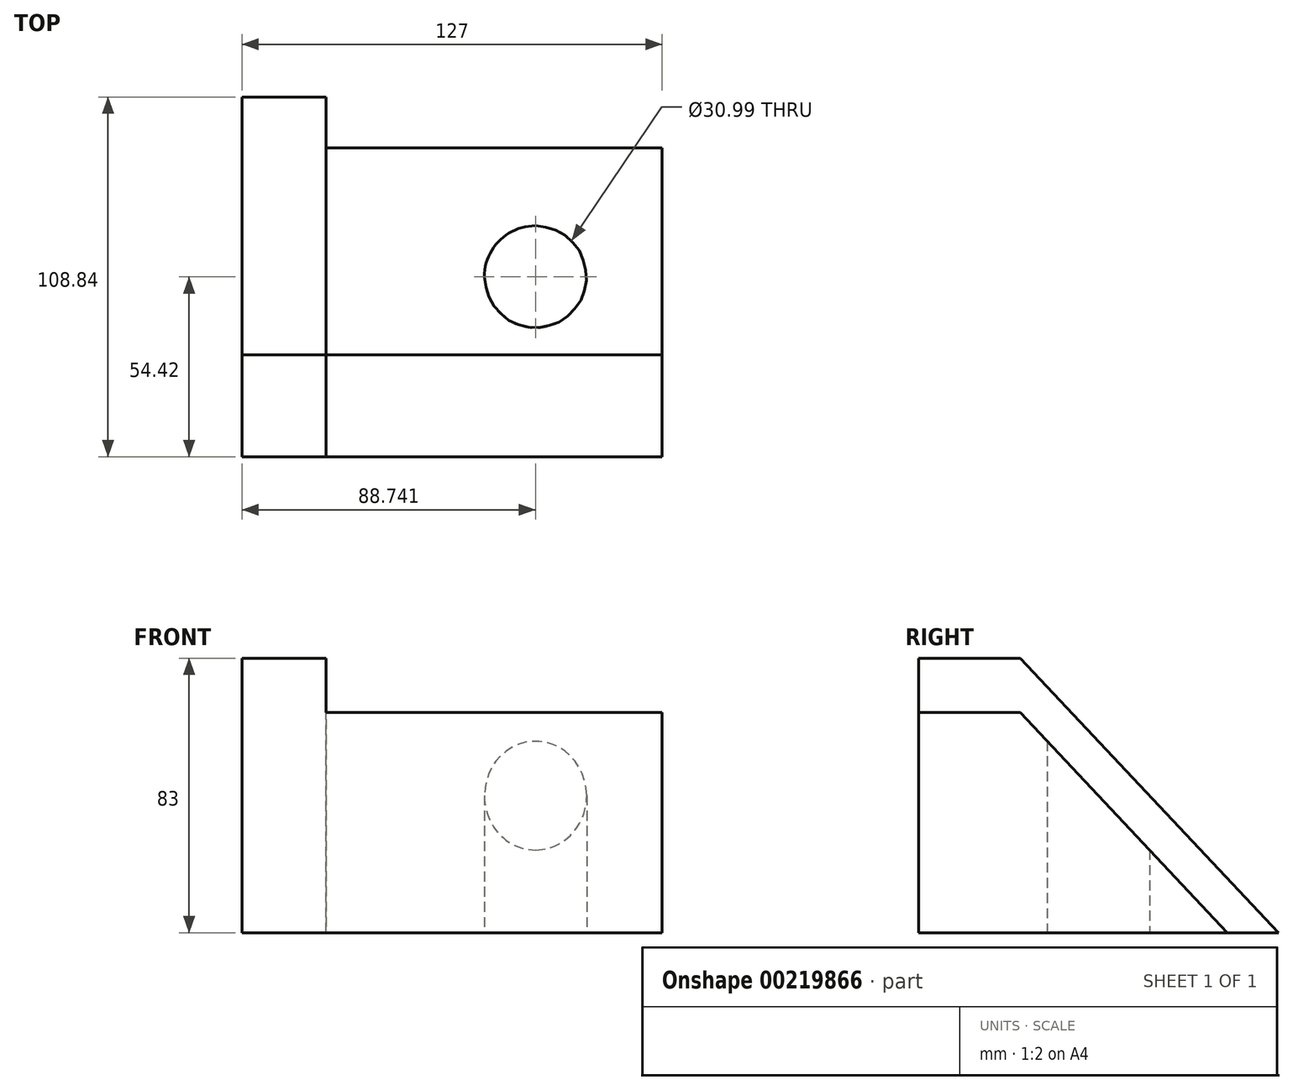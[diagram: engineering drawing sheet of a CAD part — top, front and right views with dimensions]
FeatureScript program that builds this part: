
annotation { "Feature Type Name" : "Feature", "Feature Type Description" : "" }
export const myFeature = defineFeature(function(context is Context, id is Id, definition is map)
    precondition{}
    {
        {
            var Q0;
            Q0=qCreatedBy(makeId("Right.planeOp"),FACE);
            var sketch = newSketch(context, id + "F0", { "sketchPlane" : qUnion([Q0])});
            skLineSegment(sketch, "E0.bottom", {"start": v(-54.42, 41.5) * mm, "end": v(54.42, 41.5) * mm});
            skLineSegment(sketch, "E0.top", {"start": v(-54.42, -41.5) * mm, "end": v(54.42, -41.5) * mm});
            skLineSegment(sketch, "E0.left", {"start": v(-54.42, 41.5) * mm, "end": v(-54.42, -41.5) * mm});
            skLineSegment(sketch, "E0.right", {"start": v(54.42, 41.5) * mm, "end": v(54.42, -41.5) * mm});
            skPoint(sketch, "E0.middle", {"position": v(0, 0) * mm});
            skSolve(sketch);
        }
        {
            var Q0;
            Q0 = qSketchRegion(id + "F0", true);
            extrude(context, id + "F1", {"entities" : qUnion([Q0]), "depth" : 25.4 * mm});
        }
        {
            var Q0;
            Q0=makeQuery(id+"F1.opExtrude","CAP_FACE",FACE,{"disambiguationData":[OSD([sQuery(id+"F0.wireOp",EDGE,"E0.bottom"),sQuery(id+"F0.wireOp",EDGE,"E0.top"),sQuery(id+"F0.wireOp",EDGE,"E0.left"),sQuery(id+"F0.wireOp",EDGE,"E0.right")])],"isStart":false});
            var sketch = newSketch(context, id + "F2", { "sketchPlane" : qUnion([Q0])});
            skLineSegment(sketch, "E1", {"start": v(-23.6, 41.5) * mm, "end": v(54.42, -41.5) * mm});
            skSolve(sketch);
        }
        {
            var Q0;
            {var subQ0=sQuery(id+"F2.wireOp",EDGE,"E1");Q0=makeQuery(id+"F2.imprint","IMPRINT",FACE,{"disambiguationData":[TD([[makeQuery(id+"F2.imprint","IMPRINT",EDGE,{"derivedFrom":subQ0}),1.0]])]});}
            extrude(context, id + "F3", {"entities" : qUnion([Q0]), "operationType" : NewBodyOperationType.REMOVE, "oppositeDirection" : true, "depth" : 25.4 * mm});
        }
        {
            var Q0;
            Q0=makeQuery(id+"F1.opExtrude","CAP_FACE",FACE,{"disambiguationData":[OSD([sQuery(id+"F0.wireOp",EDGE,"E0.bottom"),sQuery(id+"F0.wireOp",EDGE,"E0.top"),sQuery(id+"F0.wireOp",EDGE,"E0.left"),sQuery(id+"F0.wireOp",EDGE,"E0.right")])],"isStart":false});
            var sketch = newSketch(context, id + "F4", { "sketchPlane" : qUnion([Q0])});
            skLineSegment(sketch, "E2", {"start": v(-54.42, -41.5) * mm, "end": v(39.01, -41.5) * mm});
            skLineSegment(sketch, "E3", {"start": v(39.01, -41.5) * mm, "end": v(-23.6, 25.1) * mm});
            skLineSegment(sketch, "E4", {"start": v(-23.6, 25.1) * mm, "end": v(-54.42, 25.1) * mm});
            skLineSegment(sketch, "E5", {"start": v(-54.42, 25.1) * mm, "end": v(-54.42, -41.5) * mm});
            skSolve(sketch);
        }
        {
            var Q0;
            Q0=makeQuery(id+"F4.imprint","IMPRINT",FACE,{"disambiguationData":[TD([[makeQuery(id+"F4.imprint","IMPRINT",EDGE,{"derivedFrom":sQuery(id+"F4.wireOp",EDGE,"E2")}),1.0]])]});
            extrude(context, id + "F5", {"entities" : qUnion([Q0]), "operationType" : NewBodyOperationType.ADD, "depth" : 101.6 * mm});
        }
        {
            var Q0;
            Q0=makeQuery(id+"F5.boolean.opBoolean","MERGE",FACE,{"derivedFrom":[makeQuery(id+"F1.opExtrude","SWEPT_FACE",FACE,{"disambiguationData":[OSD([sQuery(id+"F0.wireOp",EDGE,"E0.top")])]}),makeQuery(id+"F5.opExtrude","SWEPT_FACE",FACE,{"disambiguationData":[OSD([sQuery(id+"F4.wireOp",EDGE,"E2")])]})]});
            var sketch = newSketch(context, id + "F6", { "sketchPlane" : qUnion([Q0])});
            skCircle(sketch, "E6", {"center": v(88.74, 0) * mm, "radius": 15.5 * mm});
            skSolve(sketch);
        }
        {
            var Q0;
            Q0=makeQuery(id+"F6.imprint","IMPRINT",FACE,{"disambiguationData":[TD([[makeQuery(id+"F6.imprint","IMPRINT",EDGE,{"derivedFrom":sQuery(id+"F6.wireOp",EDGE,"E6")}),1.0]])]});
            extrude(context, id + "F7", {"entities" : qUnion([Q0]), "operationType" : NewBodyOperationType.REMOVE, "endBound" : BoundingType.THROUGH_ALL, "oppositeDirection" : true, "depth" : 25.4 * mm});
        }
    });
